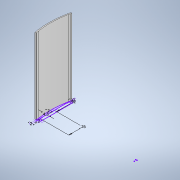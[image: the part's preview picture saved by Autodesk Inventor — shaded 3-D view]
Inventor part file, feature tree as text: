
AUTODESK INVENTOR PART (.ipt)
format: ipt  version: 2022 (Build 260153000, 153)  size: 129,024 bytes
history: native  units: mm
features: sketch x1, extrude x1
ambient origin geometry x8: Origin, YZ Plane, XZ Plane, XY Plane, X Axis, Y Axis, Z Axis, Center Point
bodies: Solid1 (feature_tree)
feature tree (2):
  sketch  "Sketch1"  dims[d15=4.5mm d17=2.0mm d18=2.0mm d19=2.0mm d20=2.0mm d21=2.0mm d22=32.0mm d24=26.0mm d33=138.0mm d34=0.0mm d35=0.5mm d36=0.872665mm d59=0.0mm d60=0.0mm d61=0.0mm d62=0.0mm]
  extrude  "Extrusion1"  Depth=138.0mm
